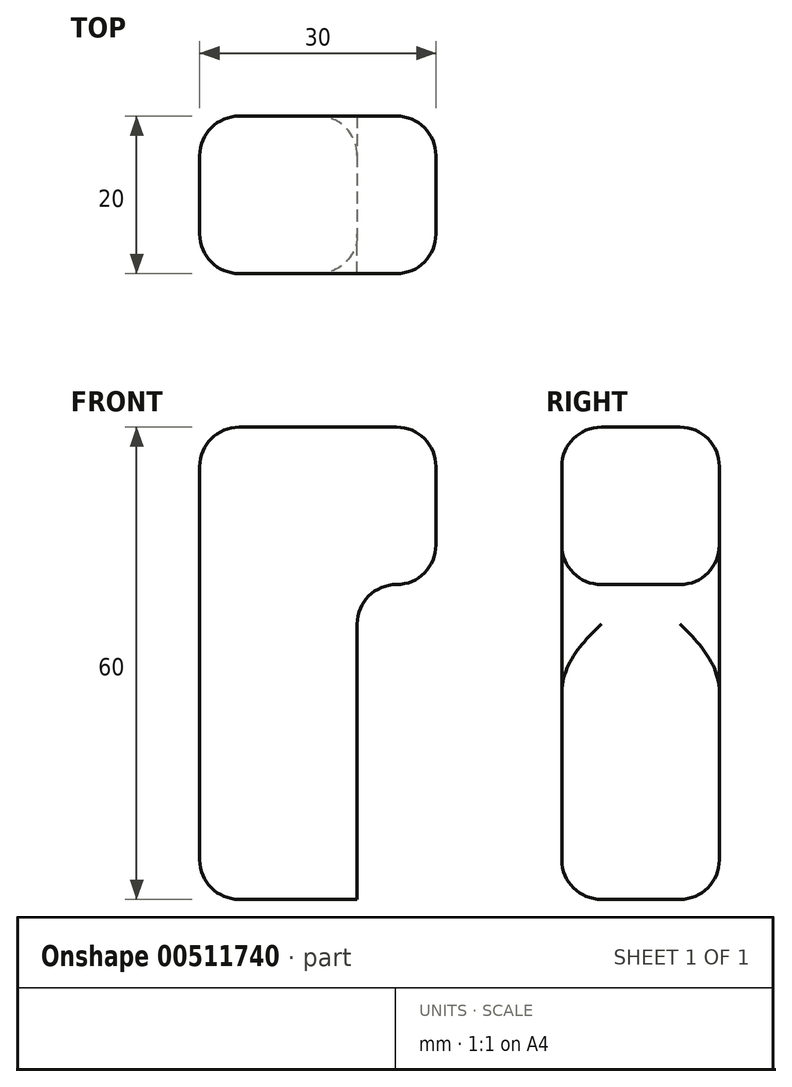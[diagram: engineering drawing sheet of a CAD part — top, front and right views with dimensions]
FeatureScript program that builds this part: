
annotation { "Feature Type Name" : "Feature", "Feature Type Description" : "" }
export const myFeature = defineFeature(function(context is Context, id is Id, definition is map)
    precondition{}
    {
        {
            var Q0;
            Q0=qCreatedBy(makeId("Top.planeOp"),FACE);
            var sketch = newSketch(context, id + "F0", { "sketchPlane" : qUnion([Q0])});
            skLineSegment(sketch, "E0.bottom", {"start": v(-15, 10) * mm, "end": v(15, 10) * mm});
            skLineSegment(sketch, "E0.top", {"start": v(-15, -10) * mm, "end": v(15, -10) * mm});
            skLineSegment(sketch, "E0.left", {"start": v(-15, 10) * mm, "end": v(-15, -10) * mm});
            skLineSegment(sketch, "E0.right", {"start": v(15, 10) * mm, "end": v(15, -10) * mm});
            skPoint(sketch, "E0.middle", {"position": v(0, 0) * mm});
            skSolve(sketch);
        }
        {
            var Q0;
            Q0 = qSketchRegion(id + "F0", true);
            extrude(context, id + "F1", {"entities" : qUnion([Q0]), "depth" : 20 * mm, "offsetDistance" : 25 * mm});
        }
        {
            var Q0;
            Q0=makeQuery(id+"F1.opExtrude","CAP_FACE",FACE,{"disambiguationData":[OSD([sQuery(id+"F0.wireOp",EDGE,"E0.bottom"),sQuery(id+"F0.wireOp",EDGE,"E0.top"),sQuery(id+"F0.wireOp",EDGE,"E0.left"),sQuery(id+"F0.wireOp",EDGE,"E0.right")])],"isStart":true});
            var sketch = newSketch(context, id + "F2", { "sketchPlane" : qUnion([Q0])});
            skLineSegment(sketch, "E1.bottom", {"start": v(-15, -10) * mm, "end": v(5, -10) * mm});
            skLineSegment(sketch, "E1.top", {"start": v(-15, 10) * mm, "end": v(5, 10) * mm});
            skLineSegment(sketch, "E1.left", {"start": v(-15, -10) * mm, "end": v(-15, 10) * mm});
            skLineSegment(sketch, "E1.right", {"start": v(5, -10) * mm, "end": v(5, 10) * mm});
            skSolve(sketch);
        }
        {
            var Q0;
            Q0 = qSketchRegion(id + "F2", true);
            extrude(context, id + "F3", {"entities" : qUnion([Q0]), "operationType" : NewBodyOperationType.ADD, "depth" : 40 * mm, "offsetDistance" : 25 * mm});
        }
        {
            var Q0;
            Q0=makeQuery(id+"F1.opExtrude","SWEPT_EDGE",EDGE,{"disambiguationData":[OSD([sQuery(id+"F0.wireOp",EDGE,"E0.bottom"),sQuery(id+"F0.wireOp",EDGE,"E0.right")])]});
            var Q1;
            Q1=makeQuery(id+"F1.opExtrude","SWEPT_EDGE",EDGE,{"disambiguationData":[OSD([sQuery(id+"F0.wireOp",EDGE,"E0.top"),sQuery(id+"F0.wireOp",EDGE,"E0.right")])]});
            var Q2;
            Q2=makeQuery(id+"F1.opExtrude","CAP_FACE",FACE,{"disambiguationData":[OSD([sQuery(id+"F0.wireOp",EDGE,"E0.bottom"),sQuery(id+"F0.wireOp",EDGE,"E0.top"),sQuery(id+"F0.wireOp",EDGE,"E0.left"),sQuery(id+"F0.wireOp",EDGE,"E0.right")])],"isStart":true});
            var Q3;
            Q3=makeQuery(id+"F3.boolean.opBoolean","MERGE",EDGE,{"derivedFrom":[makeQuery(id+"F1.opExtrude","SWEPT_EDGE",EDGE,{"disambiguationData":[OSD([sQuery(id+"F0.wireOp",EDGE,"E0.bottom"),sQuery(id+"F0.wireOp",EDGE,"E0.left")])]}),makeQuery(id+"F3.opExtrude","SWEPT_EDGE",EDGE,{"disambiguationData":[OSD([sQuery(id+"F2.wireOp",EDGE,"E1.bottom"),sQuery(id+"F2.wireOp",EDGE,"E1.left")])]})]});
            var Q4;
            Q4=makeQuery(id+"F3.boolean.opBoolean","MERGE",EDGE,{"derivedFrom":[makeQuery(id+"F1.opExtrude","SWEPT_EDGE",EDGE,{"disambiguationData":[OSD([sQuery(id+"F0.wireOp",EDGE,"E0.top"),sQuery(id+"F0.wireOp",EDGE,"E0.left")])]}),makeQuery(id+"F3.opExtrude","SWEPT_EDGE",EDGE,{"disambiguationData":[OSD([sQuery(id+"F2.wireOp",EDGE,"E1.top"),sQuery(id+"F2.wireOp",EDGE,"E1.left")])]})]});
            fillet(context, id + "F4", {"entities" : qUnion([Q0, Q1, Q2, Q3, Q4]), "radius" : 5 * mm, "tangentPropagation" : true, "allowEdgeOverflow" : false});
        }
        {
            var Q0;
            Q0=makeQuery(id+"F3.opExtrude","CAP_EDGE",EDGE,{"disambiguationData":[OSD([sQuery(id+"F2.wireOp",EDGE,"E1.top")])],"isStart":false});
            var Q1;
            Q1=makeQuery(id+"F1.opExtrude","CAP_EDGE",EDGE,{"disambiguationData":[OSD([sQuery(id+"F0.wireOp",EDGE,"E0.top")])],"isStart":false});
            fillet(context, id + "F5", {"entities" : qUnion([Q0, Q1]), "radius" : 5 * mm, "tangentPropagation" : true, "allowEdgeOverflow" : false});
        }
    });
